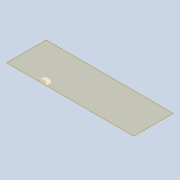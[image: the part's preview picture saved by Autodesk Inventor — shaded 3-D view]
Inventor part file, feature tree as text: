
AUTODESK INVENTOR PART (.ipt)
format: ipt  version: 2021 (Build 250183000, 183)  size: 276,992 bytes
history: native  units: in
note: dims shown in document units (in); Inventor stores cm internally (conversion verified against a paired STEP export)
features: chamfer x1
ambient origin geometry x8: Origin, YZ Plane, XZ Plane, XY Plane, X Axis, Y Axis, Z Axis, Center Point
bodies: Solid1 (feature_tree)
feature tree (1):
  chamfer  "Chamfer1"  [1 undecoded]
note: 1 required parameter value undecoded (feature->parameter linkage not recoverable at this tier; creation-order binding heuristic only, values carry confidence <= 0.55)
